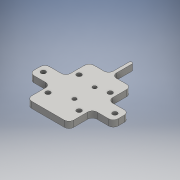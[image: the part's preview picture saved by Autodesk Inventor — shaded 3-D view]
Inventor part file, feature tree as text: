
AUTODESK INVENTOR PART (.ipt)
format: ipt  version: 2,016 SP1 (Build 200210100, 210)  size: 514,560 bytes
history: native  units: mm
features: extrude x14, sketch x12, projected_geometry x6, fillet x5, hole x1
ambient origin geometry x8: Origin, YZ Plane, XZ Plane, XY Plane, X Axis, Y Axis, Z Axis, Center Point
bodies: Solid1 (feature_tree)
feature tree (38):
  extrude  "Extrusion1"  Depth=3.0mm
  extrude  "Extrusion2"  Depth=10.0mm
  extrude  "Extrusion3"  Depth=3.0mm
  extrude  "Extrusion4"  Depth=20.0mm
  extrude  "Extrusion5"  Depth=10.0mm
  hole  "Hole1"  [1 undecoded]
  fillet  "Fillet5"  Radius=40.0mm
  fillet  "Fillet7"  Radius=10.0mm
  extrude  "Extrusion7"  Depth=4.0mm
  fillet  "Fillet9"  Radius=10.0mm
  extrude  "Extrusion8"  Depth=2.5mm
  extrude  "Extrusion10"  Depth=2.0mm
  fillet  "Fillet10"  Radius=2.0mm
  fillet  "Fillet11"  Radius=12.0mm
  extrude  "Extrusion11"  Depth=2.0mm
  extrude  "Extrusion12"  Depth=6.5mm
  extrude  "Extrusion13"  Depth=10.0mm TaperAngle=0.0deg
  extrude  "Extrusion14"  Depth=10.0mm
  extrude  "Extrusion9"  Depth=40.0mm
  extrude  "Extrusion6"  Depth=15.0mm
  sketch  "Sketch3"  dims[d0=3.0mm d1=3.0mm]
  sketch  "Sketch4"  dims[d2=20.0mm d3=10.0mm]
  sketch  "Sketch5"  dims[d4=3.0mm d5=3.0mm]
  sketch  "Sketch9"  dims[d6=20.0mm d7=20.0mm]
  sketch  "Sketch11"  dims[d8=20.0mm d9=10.0mm]
  sketch  "Sketch12"  dims[d10=30.0mm d11=15.0mm d12=40.0mm d13=10.0mm]
  projected_geometry  "Projected Loop2"
  sketch  "Sketch13"  dims[d14=4.0mm d15=0.0mm d16=4.0mm d20=10.0mm d21=0.0mm]
  projected_geometry  "Projected Loop3"
  sketch  "Sketch14"  dims[d23=2.5mm d24=2.5mm]
  sketch  "Sketch15"  dims[d25=15.0mm d26=2.0mm d27=2.0mm d28=12.0mm]
  sketch  "Sketch16"  dims[d29=2.5mm d30=6.0mm d31=4.0mm d32=2.0mm d33=90.0deg d34=8.0mm d35=20.594885mm d36=6.3mm]
  projected_geometry  "Projected Loop5"
  projected_geometry  "Projected Loop6"
  sketch  "Sketch17"  dims[d37=6.5mm d38=6.5mm]
  projected_geometry  "Projected Loop7"
  sketch  "Sketch18"  dims[d39=8.0mm d40=0.0mm d47=8.0mm d48=0.0mm d77=10.0mm d78=40.0mm d79=15.0mm d80=3.0mm d81=3.0mm d82=46.0mm d83=54.0mm d84=23.0mm d85=27.0mm d86=8.0mm d87=0.0mm d90=8.0mm d91=0.0mm d94=1.0mm d96=0.0mm d97=0.0mm d110=2.0mm d111=0.7mm d112=4.0mm d115=4.0mm d116=1.3mm d117=6.0mm d118=2.5mm d119=2.0mm d121=27.0mm d122=13.5mm d123=10.0mm d124=0.0mm d125=3.0mm d126=3.0mm d128=6.0mm d129=3.0mm d130=10.0mm d131=0.0mm d132=3.0mm d133=21.0mm d134=4.0mm d136=11.0mm d137=10.0mm d138=0.0mm d139=0.0mm d140=0.0mm d141=22.0mm d142=14.0mm d143=1.0mm d144=1.0mm d145=10.0mm d146=0.0mm d147=3.0mm d148=1.0mm d149=8.0mm d150=10.0mm d151=0.0mm d152=0.0mm d153=10.0mm d154=0.0mm d155=10.0mm d156=0.0mm d157=10.0mm d158=0.0mm]
  projected_geometry  "Projected Loop8"
note: 1 required parameter value undecoded (feature->parameter linkage not recoverable at this tier; creation-order binding heuristic only, values carry confidence <= 0.55)
